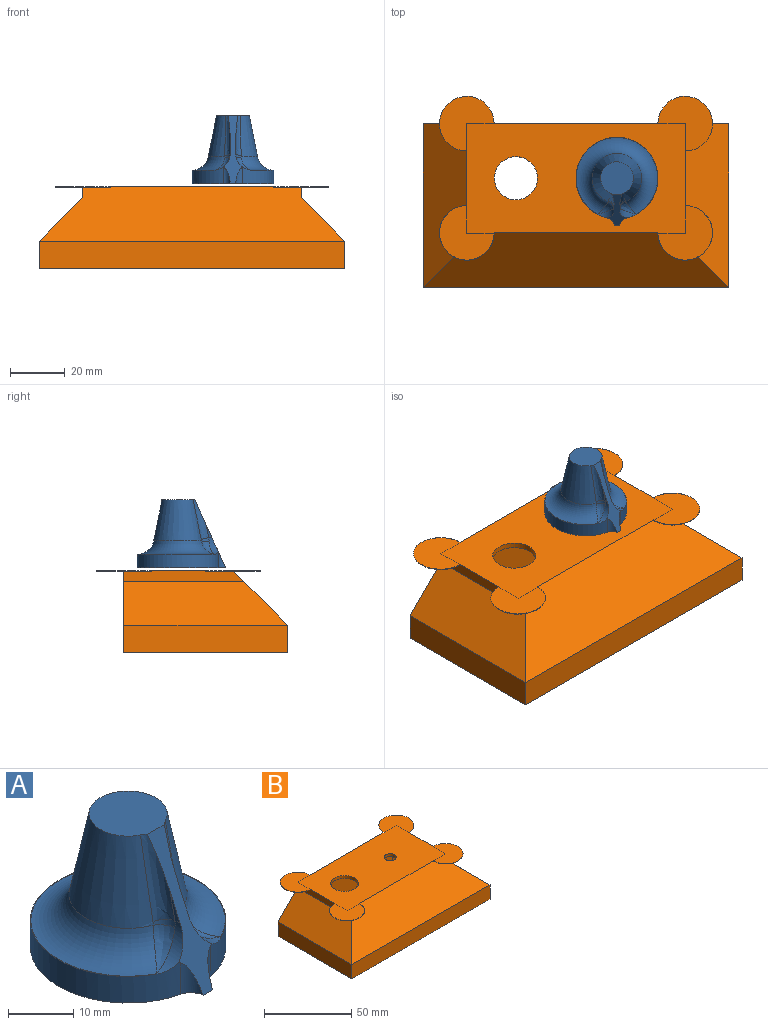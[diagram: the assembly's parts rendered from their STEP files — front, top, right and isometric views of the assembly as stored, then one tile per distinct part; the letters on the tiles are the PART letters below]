
ASSEMBLY  parts=2 mates=1
PART A: 23 faces, bbox 43.2x42x32.1 mm
  f0: plane 4.88x2.21mm, normal (-1,0,0), area 2.8mm2, adj f7,f9,f11
  f1: plane 4.88x2.21mm, normal (1,0,0), area 2.8mm2, adj f7,f8,f16
  f2: cylinder r=15mm len=30mm, axis (0,0,-1), area 440.6mm2, adj f3,f4,f7,f11,f16,f17,f18
  f3: plane 32.3x30mm, normal (0,0,-1), area 537.3mm2, adj f2,f7,f17,f18,f19
  f4: plane 30x28.27mm, normal (0,0,1), area 6.4mm2, adj f2,f11,f13,f16
  f5: cone r=6mm half-angle=11.3deg, axis (0,0,-1), area 638.6mm2, adj f6,f8,f9,f10,f13,f14
  f6: plane 12.03x12.03mm, normal (0,0,1), area 113.6mm2, adj f5,f7,f8,f9
  f7: plane 26.7x13mm, normal (0,-0.91,0.41), area 77.7mm2, adj f0,f1,f2,f3,f6,f8,f9,f11
  f8: bspline ~29.64x8.84mm, area 41mm2, adj f1,f5,f6,f7,f14
  f9: bspline ~29.64x8.84mm, area 41mm2, adj f0,f5,f6,f7,f10
  f10: bspline ~3.36x3.07mm, area 3.4mm2, adj f5,f9,f11,f12
  f11: cylinder r=6mm len=6mm, axis (0,1,0), area 16.7mm2, adj f0,f2,f4,f7,f10,f12
  f12: bspline ~6.01x5.94mm, area 11.8mm2, adj f10,f11,f13
  f13: torus R=14.92mm, axis (0,0,1), area 511mm2, adj f4,f5,f12,f15
  f14: bspline ~3.36x3.07mm, area 3.4mm2, adj f5,f8,f15,f16
  f15: bspline ~6.01x5.94mm, area 11.8mm2, adj f13,f14,f16
  f16: cylinder r=6mm len=6mm, axis (0,-1,0), area 16.7mm2, adj f1,f2,f4,f7,f14,f15
  f17: cylinder r=3mm len=5.92mm, axis (0,0,-1), area 11.2mm2, adj f2,f3,f7
  f18: cylinder r=3mm len=5.92mm, axis (0,0,-1), area 11.2mm2, adj f2,f3,f7
  f19: cylinder r=7.5mm len=15mm, axis (0,0,-1), area 141.4mm2, adj f3,f20
  f20: plane 15x15mm, normal (0,0,-1), area 148.4mm2, adj f19,f22
  f21: plane 6x6mm, normal (0,0,-1), area 28.3mm2, adj f22
  f22: cylinder r=3mm len=12mm, axis (0,0,-1), area 226.2mm2, adj f20,f21
PART B: 61 faces, bbox 112x70.1x30 mm
  f0: plane 70x25mm, normal (0,-1,0), area 1717.9mm2, adj f1,f37,f38,f39,f40,f41,f42
  f1: plane 112x60mm, normal (0,0,-1), area 1470.1mm2, adj f0,f2,f4,f8,f9,f10,f15,f16
  f2: plane 112x10mm, normal (0,-1,0), area 1120mm2, adj f1,f7,f15,f26
  f3: plane 44x4mm, normal (1,0,0), area 164mm2, adj f4,f6,f7,f32,f53,f54,f55,f56
  f4: plane 112x30mm, normal (0,1,0), area 2939.9mm2, adj f1,f3,f5,f6,f15,f21,f26,f32
  f5: plane 44x4mm, normal (-1,0,0), area 164mm2, adj f4,f6,f7,f21,f57,f58,f59,f60
  f6: plane 100x60mm, normal (0,0,1), area 3907.9mm2, adj f3,f4,f5,f7,f13,f14,f53,f56
  f7: plane 112x20mm, normal (0,-0.71,0.71), area 2619.1mm2, adj f2,f3,f5,f6,f21,f32,f55,f56
  f8: plane 76x7.93mm, normal (0,1,0), area 601mm2, adj f1,f9,f10,f44,f47,f48
  f9: plane 53x25mm, normal (-1,0,0), area 1123.6mm2, adj f1,f8,f41,f48,f49
  f10: plane 53x25mm, normal (1,0,0), area 1123.6mm2, adj f1,f8,f40,f46,f47
  f11: plane 70x32.93mm, normal (0,0,-1), area 2070.5mm2, adj f13,f14,f42,f46,f49,f52
  f12: plane 70x17.07mm, normal (0,0.71,-0.71), area 1689.9mm2, adj f44,f47,f48,f52
  f13: cylinder r=3.5mm len=7mm, axis (0,0,1), area 44mm2, adj f6,f11
  f14: cylinder r=7.9mm len=15.8mm, axis (0,0,1), area 99.3mm2, adj f6,f11
  f15: plane 60x10mm, normal (-1,0,0), area 600mm2, adj f1,f2,f4,f21
  f16: plane 12.2x4.2mm, normal (0,-1,0), area 51.2mm2, adj f1,f17,f19,f20
  f17: plane 40.4x4.2mm, normal (-1,0,0), area 169.7mm2, adj f1,f16,f18,f20
  f18: plane 12.2x4.2mm, normal (0,1,0), area 51.2mm2, adj f1,f17,f19,f20
  f19: plane 40.4x4.2mm, normal (1,0,0), area 169.7mm2, adj f1,f16,f18,f20
  f20: plane 40.4x12.2mm, normal (0,0,-1), area 479.7mm2, adj f16,f17,f18,f19,f22,f24
  f21: plane 60x16mm, normal (-0.71,0,0.71), area 1176.6mm2, adj f4,f5,f7,f15
  f22: cylinder r=1.45mm len=10mm, axis (0,0,-1), area 91.1mm2, adj f20,f23
  f23: plane 2.9x2.9mm, normal (0,0,-1), area 6.6mm2, adj f22
  f24: cylinder r=1.45mm len=10mm, axis (0,0,-1), area 91.1mm2, adj f20,f25
  f25: plane 2.9x2.9mm, normal (0,0,-1), area 6.6mm2, adj f24
  f26: plane 60x10mm, normal (1,0,0), area 600mm2, adj f1,f2,f4,f32
  f27: plane 12.2x4.2mm, normal (0,-1,0), area 51.2mm2, adj f1,f28,f30,f31
  f28: plane 40.4x4.2mm, normal (-1,0,0), area 169.7mm2, adj f1,f27,f29,f31
  f29: plane 12.2x4.2mm, normal (0,1,0), area 51.2mm2, adj f1,f28,f30,f31
  f30: plane 40.4x4.2mm, normal (1,0,0), area 169.7mm2, adj f1,f27,f29,f31
  f31: plane 40.4x12.2mm, normal (0,0,-1), area 479.7mm2, adj f27,f28,f29,f30,f33,f35
  f32: plane 60x16mm, normal (0.71,0,0.71), area 1176.6mm2, adj f3,f4,f7,f26
  f33: cylinder r=1.45mm len=10mm, axis (0,0,-1), area 91.1mm2, adj f31,f34
  f34: plane 2.9x2.9mm, normal (0,0,-1), area 6.6mm2, adj f33
  f35: cylinder r=1.45mm len=10mm, axis (0,0,-1), area 91.1mm2, adj f31,f36
  f36: plane 2.9x2.9mm, normal (0,0,-1), area 6.6mm2, adj f35
  f37: plane 3x2mm, normal (-1,0,0), area 6mm2, adj f0,f1,f4,f39
  f38: plane 3x2mm, normal (1,0,0), area 6mm2, adj f0,f1,f4,f39
  f39: cylinder r=3mm len=6mm, axis (0,-1,0), area 18.8mm2, adj f0,f4,f37,f38
  f40: cylinder r=3mm len=25mm, axis (0,0,-1), area 117.8mm2, adj f0,f1,f10,f43
  f41: cylinder r=3mm len=25mm, axis (0,0,1), area 117.8mm2, adj f0,f1,f9,f45
  f42: cylinder r=3mm len=70mm, axis (-1,0,0), area 329.9mm2, adj f0,f11,f43,f45
  f43: sphere r=3mm, area 14.1mm2, adj f40,f42,f46
  f44: cylinder r=3mm len=74.24mm, axis (-1,0,0), area 170.2mm2, adj f8,f12,f47,f48
  f45: sphere r=3mm, area 14.1mm2, adj f41,f42,f49
  f46: cylinder r=3mm len=32.93mm, axis (0,-1,0), area 155.2mm2, adj f10,f11,f43,f50
  f47: cylinder r=3mm len=22.19mm, axis (0,0.71,0.71), area 123.8mm2, adj f8,f10,f12,f44,f50
  f48: cylinder r=3mm len=22.19mm, axis (0,0.71,0.71), area 123.8mm2, adj f8,f9,f12,f44,f51
  f49: cylinder r=3mm len=32.93mm, axis (0,1,0), area 155.2mm2, adj f9,f11,f45,f51
  f50: sphere r=3mm, area 7.1mm2, adj f46,f47,f52
  f51: sphere r=3mm, area 7.1mm2, adj f48,f49,f52
  f52: cylinder r=3mm len=70mm, axis (1,0,0), area 164.9mm2, adj f11,f12,f50,f51
  f53: cylinder r=10mm len=20mm, axis (0,0,1), area 9.4mm2, adj f3,f4,f6,f54
  f54: plane 20x20mm, normal (0,0,-1), area 235.6mm2, adj f3,f4,f53
  f55: plane 20x20mm, normal (0,0,-1), area 233.6mm2, adj f3,f7,f56
  f56: cylinder r=10mm len=20mm, axis (0,0,1), area 9.4mm2, adj f3,f6,f7,f55
  f57: cylinder r=10mm len=20mm, axis (0,0,1), area 9.4mm2, adj f4,f5,f6,f58
  f58: plane 20x20mm, normal (0,0,-1), area 235.6mm2, adj f4,f5,f57
  f59: cylinder r=10mm len=20mm, axis (0,0,1), area 9.4mm2, adj f5,f6,f7,f60
  f60: plane 20x20mm, normal (0,0,-1), area 233.6mm2, adj f5,f7,f59
PLACE A t=(5.85,10.56,12.89)mm
PLACE B t=(-9.15,0.56,-18.11)mm
MATE fastened A.f2 <-> B.f13  axis (0,0,-1) through (5.85,10.56,12.89)mm
